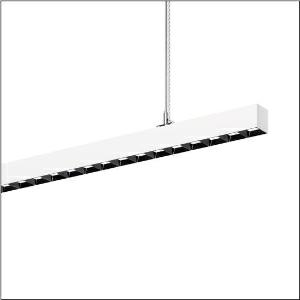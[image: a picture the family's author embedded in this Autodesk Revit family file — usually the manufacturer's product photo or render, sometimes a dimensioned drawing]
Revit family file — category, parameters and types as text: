
# Revit family: silica_r__21_51mx32dc4dwb_0a61
name_source: partatom
category: Lighting Fixtures
units: mm (PartAtom-declared; Revit-internal decimal feet)

## family parameters
Cut with Voids When Loaded = No
Host = Face
Light Source = No
Part Type = Normal
Room Calculation Point = No
Round Connector Dimension = Use Diameter
Shared = No

## types (1)
- --- (1 x LED, 18230 lm, 105.8 W, 4000K)
    Apparent Load = 106 VA
    CIE Flux Codes = 86 99 100 59 100
    Color Rendering = 80
    Color Temperature = 4000K
    Default Elevation = 1800 mm
    Description = Silica® 21, office luminaire, primary light control with darklight reflector, of PMMA, black, CAT 2 (L<= 3000cd/m²), light emission: direct/indirect distribution, primary light characteristic: symmetric, installation type: suspended mounting, LED, rated luminous flux: 18.230lm, luminous efficacy: 172lm/W, light colour: 840, colour temperature: 4000K, with terminal, 3+2-pole, max. 2.5mm², mains connection: 220..240V, AC, 50/60Hz, rated input power: 105.8W, luminaire housing, of aluminium, traffic white (RAL 9016), length: 3.004mm, width: 53mm, height: 53mm, protection rating (complete): IP20, insulation class (complete): insulation class I (protective earthing), certification: CE, permissible operating ambient temperature: 0..+35°C, standard: EN 50419, packaging unit: 1 piece
    Height = 53 mm
    Lamp = 1 x LED
    Lamp Light Flux = 18230 lm
    Lamp Power = 105.8 W
    Lamp count = 1
    Length = 3004 mm
    Luminous efficacy = 172 lm/W
    Manufacturer = Siteco
    ModVariant = No
    Model = 51MX32DC4DWB
    Mounting Place = Ceiling
    Mounting Type = Pendant
    Number of Poles = 1
    OnlyDefault = Yes
    Power Factor = 1
    Product Name = Silica® 21
    Product group = office luminaire | ceiling pendant
    ProductGroupID = 902
    Protection Class = Protection class I
    Protection Degree = IP 20
    RLX_Detail_Level = 1
    RLX_Emergency_Light_Flux = 0 lm
    RLX_Emergency_Type = 0
    RLX_Emergency_Type_DB = No
    RlxData = <blob elided: 64297 chars, md5=12dba25d>
    Socket = socket
    Standby Power = 0 W
    System Light Flux = 18230 lm
    System Power = 106 W
    Type Comments = factory setting: luminous flux: 100 % | dim-lin: 254 | 366 mA
    Type Image = l_1335871.jpg
    URL = http://relux.com
    VarID = @adj_091739
    Voltage = 0 V
    Weight = 0.00 kg
    Width = 53 mm

## geometry (parser evidence)
native form markers: Blend x4, Sweep x12
no freeform markers — native parametric forms only
